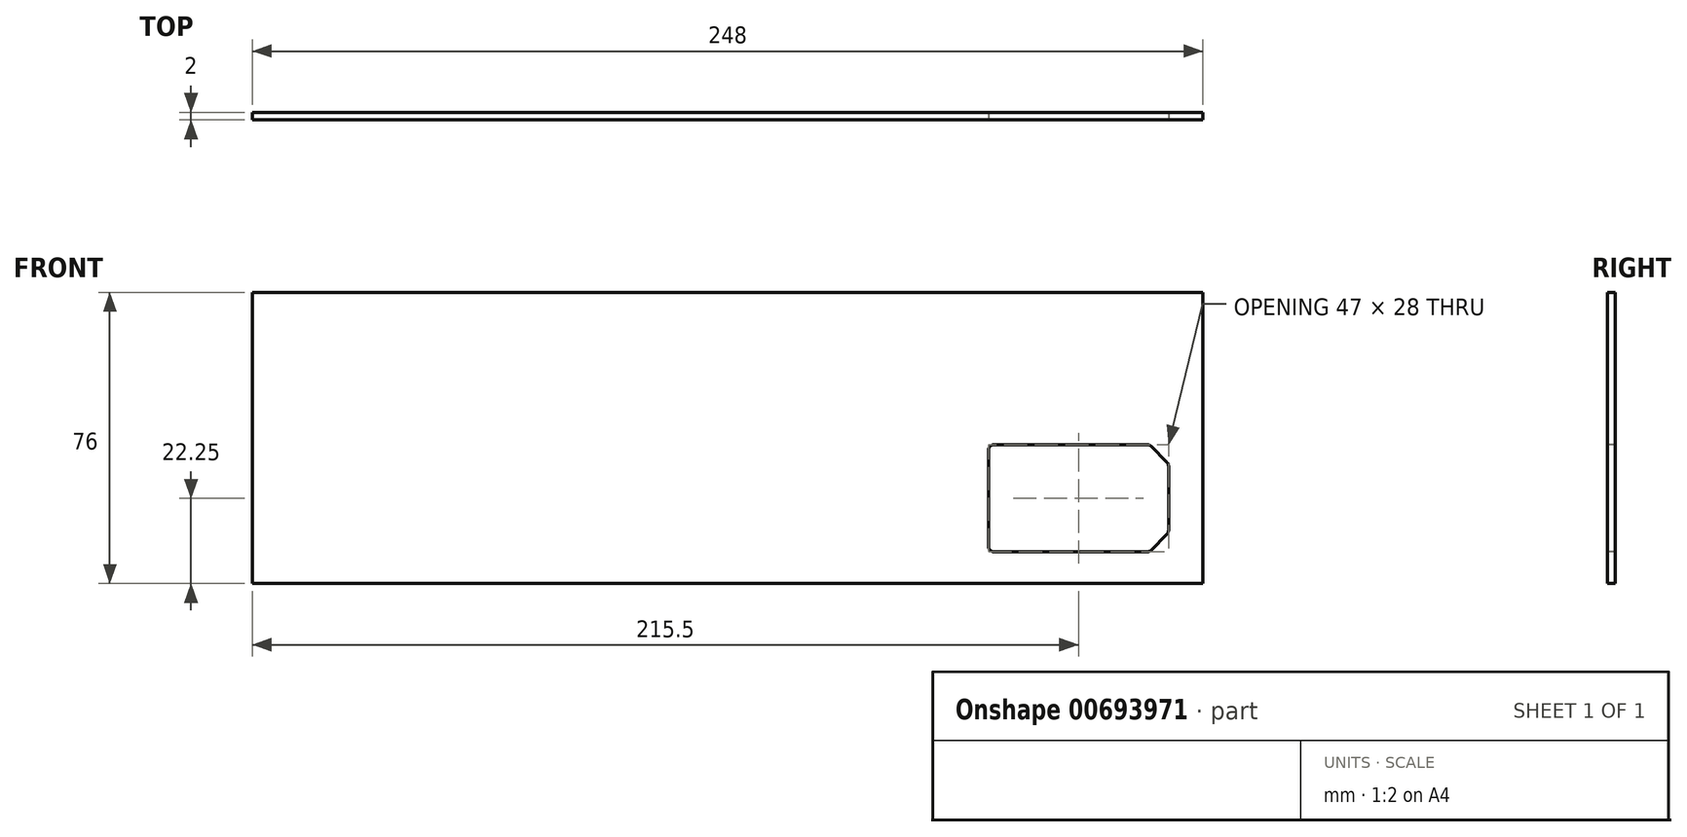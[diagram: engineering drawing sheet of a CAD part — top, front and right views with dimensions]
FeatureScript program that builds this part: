
annotation { "Feature Type Name" : "Feature", "Feature Type Description" : "" }
export const myFeature = defineFeature(function(context is Context, id is Id, definition is map)
    precondition{}
    {
        {
            var Q0;
            Q0=qCreatedBy(makeId("Front.planeOp"),FACE);
            var sketch = newSketch(context, id + "F0", { "sketchPlane" : qUnion([Q0])});
            skLineSegment(sketch, "E0.bottom", {"start": v(124, 38) * mm, "end": v(-124, 38) * mm});
            skLineSegment(sketch, "E0.top", {"start": v(124, -38) * mm, "end": v(-124, -38) * mm});
            skLineSegment(sketch, "E0.left", {"start": v(124, 38) * mm, "end": v(124, -38) * mm});
            skLineSegment(sketch, "E0.right", {"start": v(-124, 38) * mm, "end": v(-124, -38) * mm});
            skPoint(sketch, "E0.middle", {"position": v(0, 0) * mm});
            skLineSegment(sketch, "E1.bottom", {"start": v(69.5, -1.75) * mm, "end": v(109.38, -1.75) * mm});
            skLineSegment(sketch, "E1.top", {"start": v(69.5, -29.75) * mm, "end": v(109.38, -29.75) * mm});
            skLineSegment(sketch, "E1.left", {"start": v(68, -3.25) * mm, "end": v(68, -28.25) * mm});
            skLineSegment(sketch, "E1.right", {"start": v(115, -7.37) * mm, "end": v(115, -24.13) * mm});
            skLineSegment(sketch, "E2", {"start": v(110.44, -2.19) * mm, "end": v(114.56, -6.31) * mm});
            skLineSegment(sketch, "E3", {"start": v(68, -15.75) * mm, "end": v(115, -15.75) * mm, "construction": true});
            skLineSegment(sketch, "E4.MirrorCS", {"start": v(110.44, -29.31) * mm, "end": v(114.56, -25.19) * mm});
            skPoint(sketch, "E5.visualSharp", {"position": v(68, -1.75) * mm});
            skArc(sketch, "E5.filletArc", {"start": v(69.5, -1.75) * mm, "mid": v(68.44, -2.19) * mm, "end": v(68, -3.25) * mm});
            skPoint(sketch, "E6.visualSharp", {"position": v(68, -29.75) * mm});
            skArc(sketch, "E6.filletArc", {"start": v(68, -28.25) * mm, "mid": v(68.44, -29.31) * mm, "end": v(69.5, -29.75) * mm});
            skPoint(sketch, "E7.newPointA", {"position": v(115, -1.75) * mm});
            skPoint(sketch, "E7.newPointB", {"position": v(110, -1.75) * mm});
            skArc(sketch, "E7.filletArc", {"start": v(110.44, -2.19) * mm, "mid": v(109.95, -1.86) * mm, "end": v(109.38, -1.75) * mm});
            skPoint(sketch, "E8.newPointA", {"position": v(115, -6.75) * mm});
            skArc(sketch, "E8.filletArc", {"start": v(115, -7.37) * mm, "mid": v(114.89, -6.8) * mm, "end": v(114.56, -6.31) * mm});
            skPoint(sketch, "E9.newPointA", {"position": v(115, -29.75) * mm});
            skPoint(sketch, "E9.newPointB", {"position": v(115, -24.75) * mm});
            skArc(sketch, "E9.filletArc", {"start": v(114.56, -25.19) * mm, "mid": v(114.89, -24.7) * mm, "end": v(115, -24.13) * mm});
            skPoint(sketch, "E10.newPointB", {"position": v(110, -29.75) * mm});
            skArc(sketch, "E10.filletArc", {"start": v(109.38, -29.75) * mm, "mid": v(109.95, -29.64) * mm, "end": v(110.44, -29.31) * mm});
            skSolve(sketch);
        }
        {
            var Q0;
            Q0 = qSketchRegion(id + "F0", true);
            var Q1;
            {var subQ3=sQuery(id+"F0.wireOp",EDGE,"E2");Q1=makeQuery(id+"F0.imprint","IMPRINT",FACE,{"disambiguationData":[TD([[makeQuery(id+"F0.imprint","IMPRINT",EDGE,{"derivedFrom":subQ3}),1.0]])]});}
            var Q2;
            {var subQ3=sQuery(id+"F0.wireOp",EDGE,"E4.MirrorCS");Q2=makeQuery(id+"F0.imprint","IMPRINT",FACE,{"disambiguationData":[TD([[makeQuery(id+"F0.imprint","IMPRINT",EDGE,{"derivedFrom":subQ3}),-1.0]])]});}
            extrude(context, id + "F1", {"entities" : qUnion([Q0, Q1, Q2]), "oppositeDirection" : true, "depth" : 2 * mm, "offsetDistance" : 25 * mm});
        }
    });
